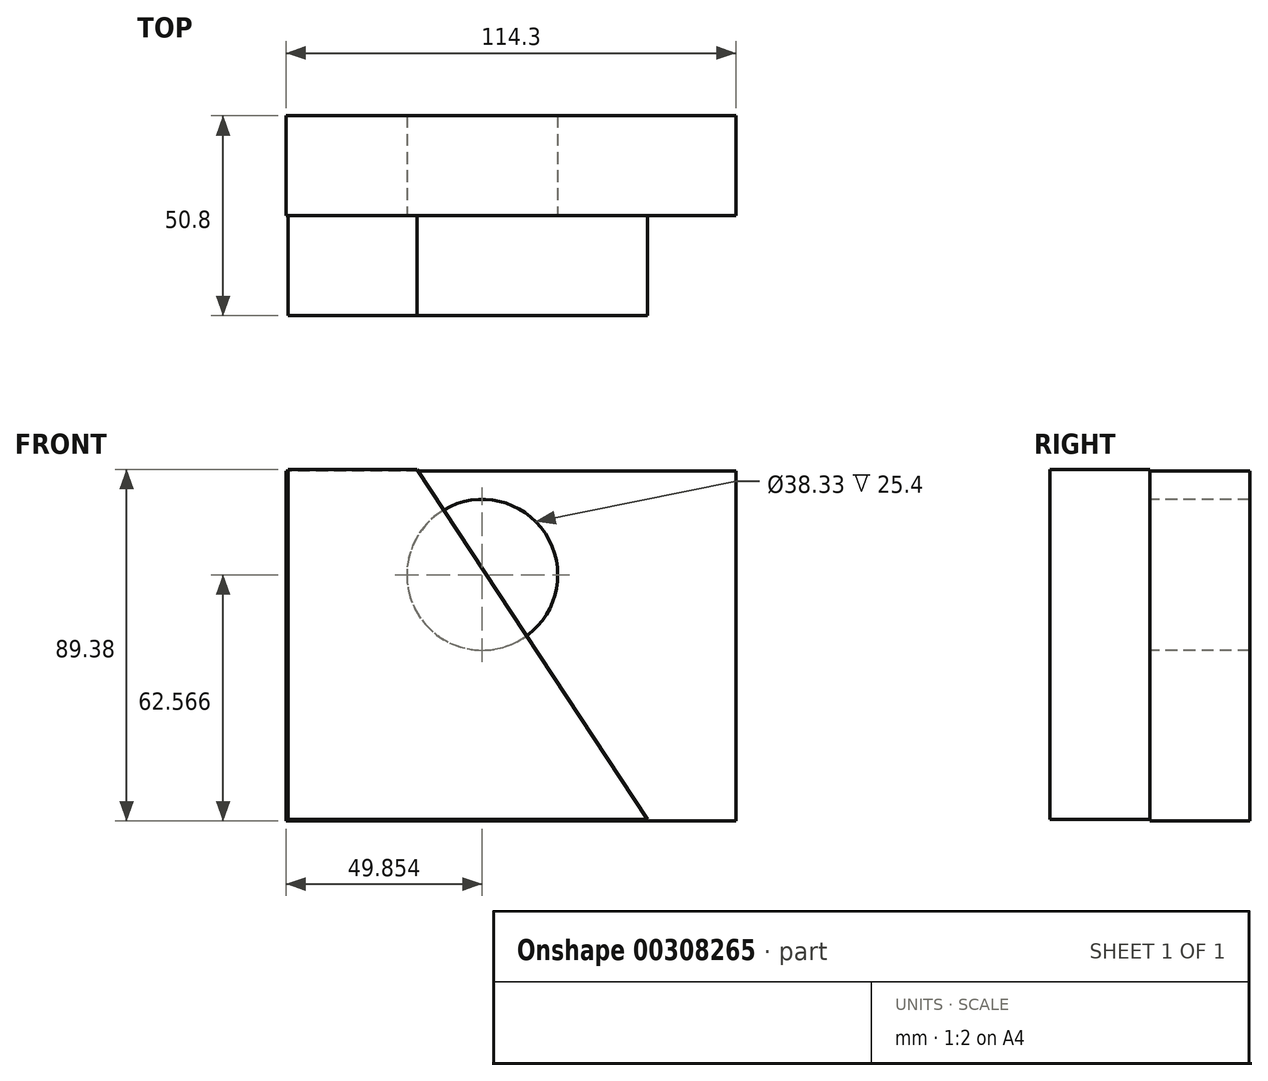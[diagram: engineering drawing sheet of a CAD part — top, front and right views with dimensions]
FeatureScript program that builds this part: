
annotation { "Feature Type Name" : "Feature", "Feature Type Description" : "" }
export const myFeature = defineFeature(function(context is Context, id is Id, definition is map)
    precondition{}
    {
        {
            var Q0;
            Q0=qCreatedBy(makeId("Front.planeOp"),FACE);
            var sketch = newSketch(context, id + "F0", { "sketchPlane" : qUnion([Q0])});
            skLineSegment(sketch, "E0", {"start": v(-74.1, 37.03) * mm, "end": v(-74.1, -51.87) * mm});
            skLineSegment(sketch, "E1", {"start": v(-74.1, -51.87) * mm, "end": v(40.2, -51.87) * mm});
            skLineSegment(sketch, "E2", {"start": v(40.2, -51.87) * mm, "end": v(40.2, 37.03) * mm});
            skLineSegment(sketch, "E3", {"start": v(40.2, 37.03) * mm, "end": v(-74.1, 37.03) * mm});
            skSolve(sketch);
        }
        {
            var Q0;
            Q0 = qSketchRegion(id + "F0", true);
            extrude(context, id + "F1", {"entities" : qUnion([Q0]), "oppositeDirection" : true, "depth" : 25.4 * mm});
        }
        {
            var Q0;
            Q0=qCreatedBy(makeId("Front.planeOp"),FACE);
            var sketch = newSketch(context, id + "F2", { "sketchPlane" : qUnion([Q0])});
            skLineSegment(sketch, "E4", {"start": v(-40.79, 37.5) * mm, "end": v(17.68, -51.49) * mm});
            skLineSegment(sketch, "E5", {"start": v(17.68, -51.49) * mm, "end": v(-73.6, -51.49) * mm});
            skLineSegment(sketch, "E6", {"start": v(-73.6, -51.49) * mm, "end": v(-73.6, 37.5) * mm});
            skLineSegment(sketch, "E7", {"start": v(-73.6, 37.5) * mm, "end": v(-40.79, 37.5) * mm});
            skSolve(sketch);
        }
        {
            var Q0;
            Q0 = qSketchRegion(id + "F2", true);
            extrude(context, id + "F3", {"entities" : qUnion([Q0]), "operationType" : NewBodyOperationType.ADD, "depth" : 25.4 * mm});
        }
        {
            var Q0;
            Q0=qCreatedBy(makeId("Front.planeOp"),FACE);
            var sketch = newSketch(context, id + "F4", { "sketchPlane" : qUnion([Q0])});
            skCircle(sketch, "E8", {"center": v(-24.25, 10.7) * mm, "radius": 19.16 * mm});
            skSolve(sketch);
        }
        {
            var Q0;
            Q0 = qSketchRegion(id + "F4", true);
            extrude(context, id + "F5", {"entities" : qUnion([Q0]), "operationType" : NewBodyOperationType.REMOVE, "oppositeDirection" : true, "depth" : 50.8 * mm});
        }
    });
